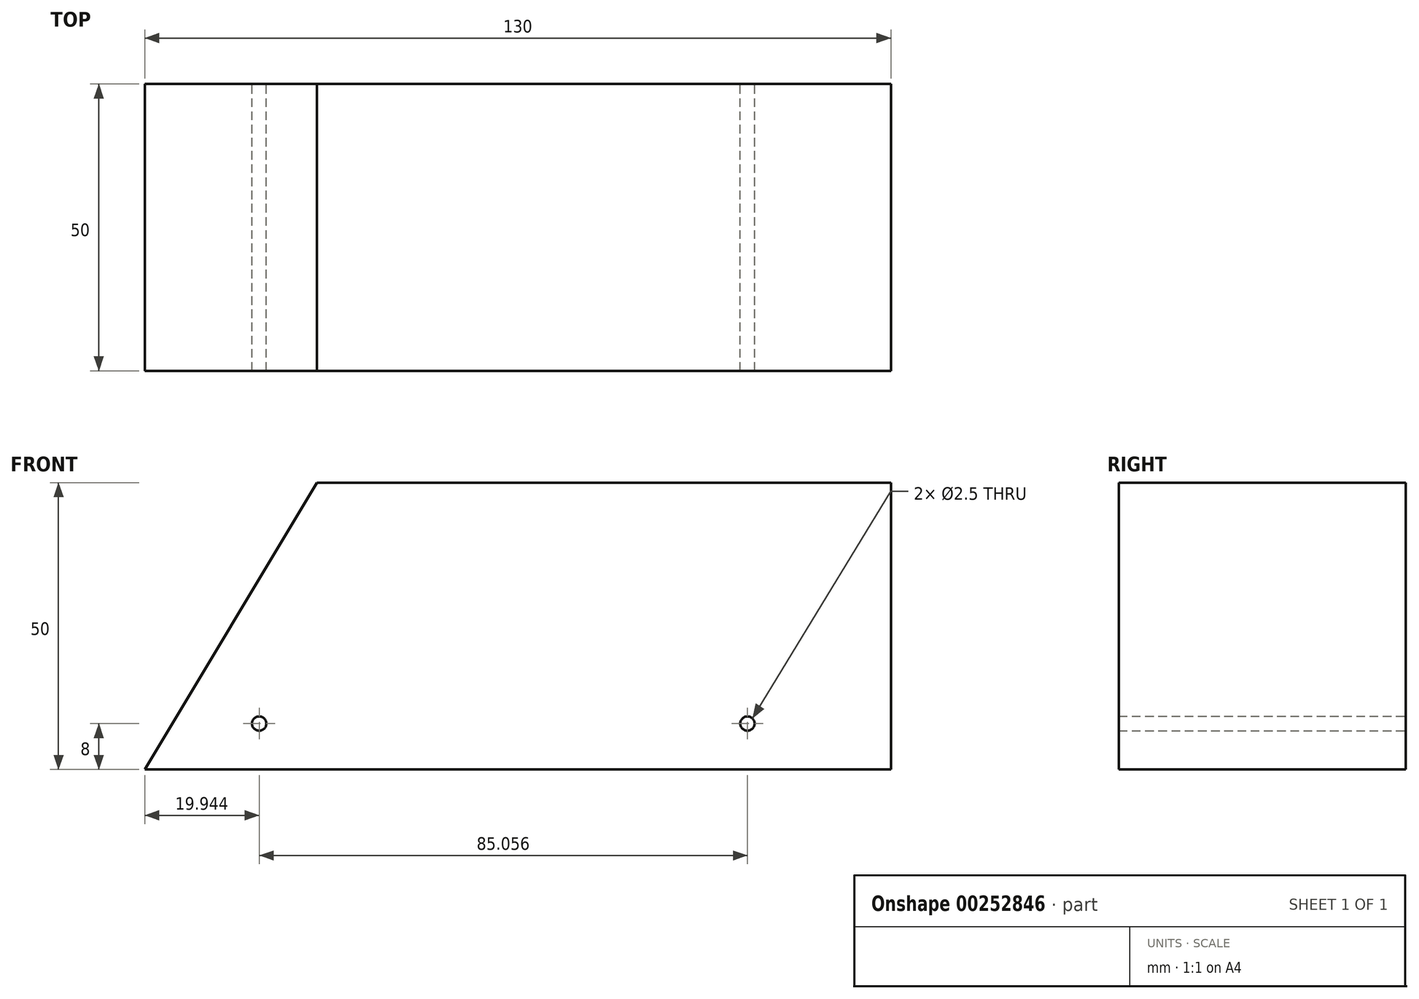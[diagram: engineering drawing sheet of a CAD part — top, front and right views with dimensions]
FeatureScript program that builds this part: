
annotation { "Feature Type Name" : "Feature", "Feature Type Description" : "" }
export const myFeature = defineFeature(function(context is Context, id is Id, definition is map)
    precondition{}
    {
        {
            var Q0;
            Q0=qCreatedBy(makeId("Front.planeOp"),FACE);
            var sketch = newSketch(context, id + "F0", { "sketchPlane" : qUnion([Q0])});
            skLineSegment(sketch, "E0.top", {"start": v(50, 25) * mm, "end": v(-50, 25) * mm});
            skLineSegment(sketch, "E0.left", {"start": v(50, -25) * mm, "end": v(50, 25) * mm});
            skPoint(sketch, "E0.middle", {"position": v(0, 0) * mm});
            skLineSegment(sketch, "E1", {"start": v(-80, -25) * mm, "end": v(-50, 25) * mm});
            skLineSegment(sketch, "E2", {"start": v(-80, -25) * mm, "end": v(50, -25) * mm});
            skLineSegment(sketch, "E3", {"start": v(50, -25) * mm, "end": v(25, -25) * mm});
            skCircle(sketch, "E4", {"center": v(-60.06, -17) * mm, "radius": 1.25 * mm});
            skCircle(sketch, "E5", {"center": v(25, -17) * mm, "radius": 1.25 * mm});
            skSolve(sketch);
        }
        {
            var Q0;
            Q0=makeQuery(id+"F0.imprint","IMPRINT",FACE,{"disambiguationData":[TD([[makeQuery(id+"F0.imprint","IMPRINT",EDGE,{"derivedFrom":sQuery(id+"F0.wireOp",EDGE,"E0.top")}),1.0]])]});
            extrude(context, id + "F1", {"entities" : qUnion([Q0]), "depth" : 50 * mm});
        }
    });
